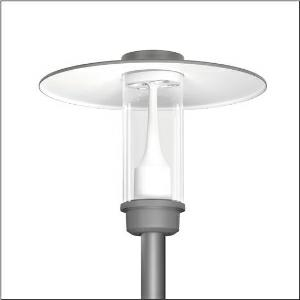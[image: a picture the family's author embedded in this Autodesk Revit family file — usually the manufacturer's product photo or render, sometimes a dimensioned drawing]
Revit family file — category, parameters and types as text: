
# Revit family: litepole_2_iq___st1_2a_5xa5425mf14hp_68c7
name_source: partatom
category: Lighting Fixtures
units: mm (PartAtom-declared; Revit-internal decimal feet)

## family parameters
Cut with Voids When Loaded = No
Host = Face
Light Source = No
Part Type = Normal
Room Calculation Point = No
Round Connector Dimension = Use Diameter
Shared = No

## types (1)
- --- (1 x LED, 4270 lm, 33.6 W, 2700K)
    Apparent Load = 34 VA
    CIE Flux Codes = 22 59 92 98 100
    Color Rendering = 70
    Color Temperature = 2700K
    Default Elevation = 1800 mm
    Description = Litepole 2 iQ, mast luminaire, Module 540 iQ-SR, primary light control with 3 zone facetted reflector, of plastic, silver coated, highly specular, structured, primary optical cover: cover, of PMMA, transparent, light distribution: ST1.2a, light emission: direct distribution, primary light characteristic: asymmetric, installation type: post-top, LED, High Power LED, rated luminous flux: 4.270lm, luminous efficacy: 127lm/W, light colour: 727, colour temperature: 2700K, control gear: iQ Street-Remote, control: pre-setting: logarithmic dimming characteristic, Street-Remote, Auto-Match, Temp-Guard, Lumen-Switch, Night-Set, Smart-Wire, Light-Fading, Desk-Remote (wireless, voltage-free reading and setting of iQ features in the workshop via application-optimized NFC function/RFID function), optimised constant luminous flux control (CLO 2.0), with terminal, 6-pole, max. 2.5mm², mains connection: 230..240V, AC, 50/60Hz, start of lifetime: 34W, end of service life: 36W, reduction: 15W, luminaire housing, upper part, of aluminium, coated, Siteco® metallic grey (DB 702S), diameter: 750mm, height: 590mm, spigot size: d x l = 76 x 70mm (post-top) | with reducer (optional accessory) 60 x 70mm, mounting height: 3..5m, post-top mast mounting element, of diecast aluminium, coated, Siteco® metallic grey (DB 702S), Module 540 iQ-SR, traffic white (RAL 9016), equipment: Power, protection rating (complete): IP65, insulation class (complete): insulation class II (safety insulation), certification: CE, ENEC, VDE, packaging unit: 1 piece

Light Distribution: ST1.2a
    Height = 590 mm
    Lamp = 1 x LED
    Lamp Light Flux = 4270 lm
    Lamp Power = 33.6 W
    Lamp count = 1
    Length = 750 mm
    Luminous efficacy = 127 lm/W
    Manufacturer = Siteco
    ModVariant = No
    Model = 5XA5425MF14HP
    Number of Poles = 1
    OnlyDefault = Yes
    Power Factor = 1
    Product Name = Litepole 2 iQ | ST1.2a
    Product group = mast luminaire | pylon top
    ProductGroupID = 6100
    Protection Class = Protection class II
    Protection Degree = IP 65
    RLX_Detail_Level = 1
    RLX_Emergency_Light_Flux = 0 lm
    RLX_Emergency_Type = 0
    RLX_Emergency_Type_DB = No
    RlxData = <blob elided: 31969 chars, md5=efd43e4e>
    Socket = socket
    Standby Power = 0 W
    System Light Flux = 4270 lm
    System Power = 34 W
    Type Comments = factory setting: luminous flux: 100 % | dim-lin: 254 | 695 mA
    Type Image = l_1006518.jpg
    URL = http://relux.com
    VarID = @adj_173805
    Voltage = 0 V
    Weight = 0.00 kg
    Width = 0 mm  [stored 0 ft]

note: [stored X ft] marks values corroborated as IEEE doubles in the binary element streams (Revit-internal decimal feet)

## geometry (parser evidence)
native form markers: Blend x4, Sweep x9
no freeform markers — native parametric forms only
